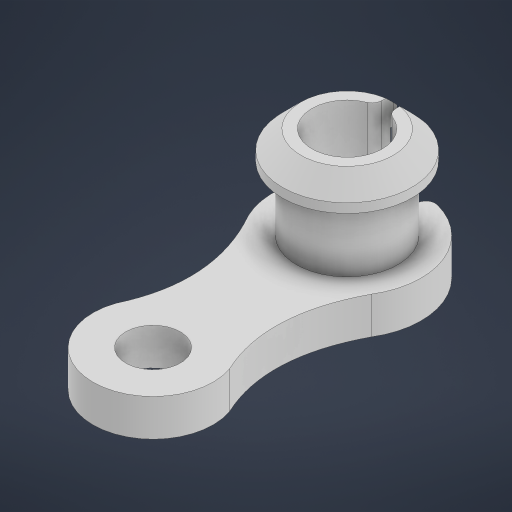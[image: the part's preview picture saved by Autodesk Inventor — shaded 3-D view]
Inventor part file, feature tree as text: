
AUTODESK INVENTOR PART (.ipt)
format: ipt  version: 2024 (Build 280153000, 153)  size: 262,656 bytes
history: native  units: in
note: dims shown in document units (in); Inventor stores cm internally (conversion verified against a paired STEP export)
features: extrude x4, sketch x3, projected_geometry x2, chamfer x1, fillet x1
ambient origin geometry x8: Origin, YZ Plane, XZ Plane, XY Plane, X Axis, Y Axis, Z Axis, Center Point
bodies: Solid1 (feature_tree)
feature tree (11):
  extrude  "Extrusion1"  Depth=0.5118in
  sketch  "Sketch2"  dims[d2=0.6299in d3=0.8268in]
  extrude  "Extrusion2"  Depth=0.8268in
  extrude  "Extrusion3"  Depth=0.0394in
  extrude  "Extrusion4"  Depth=0.0394in
  chamfer  "Chamfer1"  Distance=0.1969in
  fillet  "Fillet1"  Radius=0.2756in
  sketch  "Sketch1"  dims[d0=0.2323in d1=0.5118in]
  projected_geometry  "Projected Loop1"
  sketch  "Sketch4"  dims[d4=0.1575in d5=0.0in d6=0.4331in d7=0.0591in d8=0.1969in d9=0.0in d10=0.2756in d11=0.0in d12=0.0591in d13=0.1181in d14=0.0in d15=0.0787in d16=0.125in d17=45.0deg d18=0.0394in]
  projected_geometry  "Projected Loop4"
